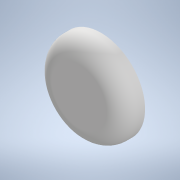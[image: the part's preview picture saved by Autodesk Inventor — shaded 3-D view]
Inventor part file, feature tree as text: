
AUTODESK INVENTOR PART (.ipt)
format: ipt  version: 2020.2 (Build 242310000, 310)  size: 119,808 bytes
history: native  units: in
note: dims shown in document units (in); Inventor stores cm internally (conversion verified against a paired STEP export)
features: revolve x1, fillet x1, sketch x1
ambient origin geometry x8: Origin, YZ Plane, XZ Plane, XY Plane, X Axis, Y Axis, Z Axis, Center Point
bodies: Solid1 (feature_tree)
feature tree (3):
  revolve  "Revolution1"  [1 undecoded]
  fillet  "Fillet1"  [1 undecoded]
  sketch  "Sketch1"  dims[d0=1.5748in d1=0.7874in d2=90.0deg d3=0.5906in]
note: 2 required parameter values undecoded (feature->parameter linkage not recoverable at this tier; creation-order binding heuristic only, values carry confidence <= 0.55)